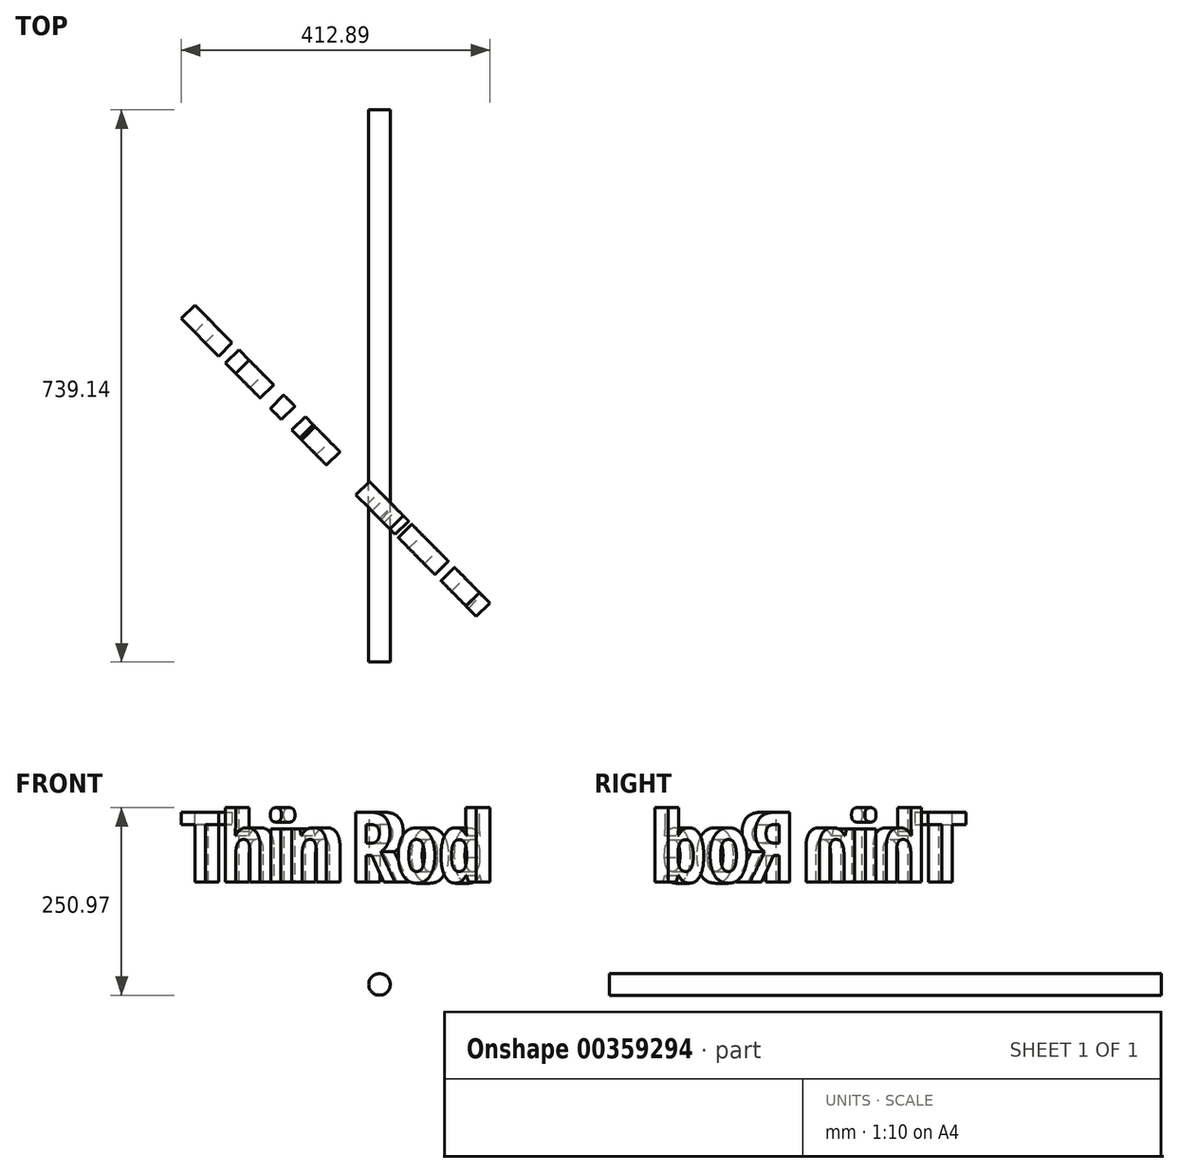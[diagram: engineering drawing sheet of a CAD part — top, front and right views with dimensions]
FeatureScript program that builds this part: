
annotation { "Feature Type Name" : "Feature", "Feature Type Description" : "" }
export const myFeature = defineFeature(function(context is Context, id is Id, definition is map)
    precondition{}
    {
        {
            var Q0;
            Q0=qCreatedBy(makeId("Front.planeOp"),FACE);
            var sketch = newSketch(context, id + "F0", { "sketchPlane" : qUnion([Q0])});
            skCircle(sketch, "E0", {"center": v(0, 0) * mm, "radius": 14.45 * mm});
            skSolve(sketch);
        }
        {
            var Q0;
            Q0=makeQuery(id+"F0.imprint","IMPRINT",FACE,{"disambiguationData":[TD([[makeQuery(id+"F0.imprint","IMPRINT",EDGE,{"derivedFrom":sQuery(id+"F0.wireOp",EDGE,"E0")}),1.0]])]});
            extrude(context, id + "F1", {"entities" : qUnion([Q0]), "depth" : 386.08 * mm, "hasSecondDirection" : true, "secondDirectionOppositeDirection" : true, "secondDirectionDepth" : 353.06 * mm});
        }
        {
            var Q0;
            Q0=qCreatedBy(makeId("Top.planeOp"),FACE);
            var sketch = newSketch(context, id + "F2", { "sketchPlane" : qUnion([Q0])});
            skLineSegment(sketch, "E1", {"start": v(0, 0) * mm, "end": v(-158.06, -156.63) * mm});
            skSolve(sketch);
        }
        {
            var Q0;
            Q0=sQuery(id+"F2.wireOp",EDGE,"E1");
            cPlane(context, id + "F3", {"entities" : qUnion([Q0]), "cplaneType" : CPlaneType.MID_PLANE, "offset" : 25.4 * mm, "flipAlignment" : true, "width" : 152.4 * mm, "height" : 152.4 * mm});
        }
        {
            var Q0;
            Q0=qCreatedBy(id+"F3.planeOp",FACE);
            var sketch = newSketch(context, id + "F4", { "sketchPlane" : qUnion([Q0])});
            skText(sketch, "E2", { "text": "Thin Rod", "fontName": "OpenSans-Bold.ttf"});
            const initialGuessF4  = {"E2": [-0.24162, 0.13677, 1, 0, 0.09452]};
            skSetInitialGuess(sketch, initialGuessF4);
            skSolve(sketch);
        }
        {
            var Q0;
            Q0 = qSketchRegion(id + "F4", true);
            extrude(context, id + "F5", {"entities" : qUnion([Q0]), "depth" : 25.4 * mm});
        }
    });
